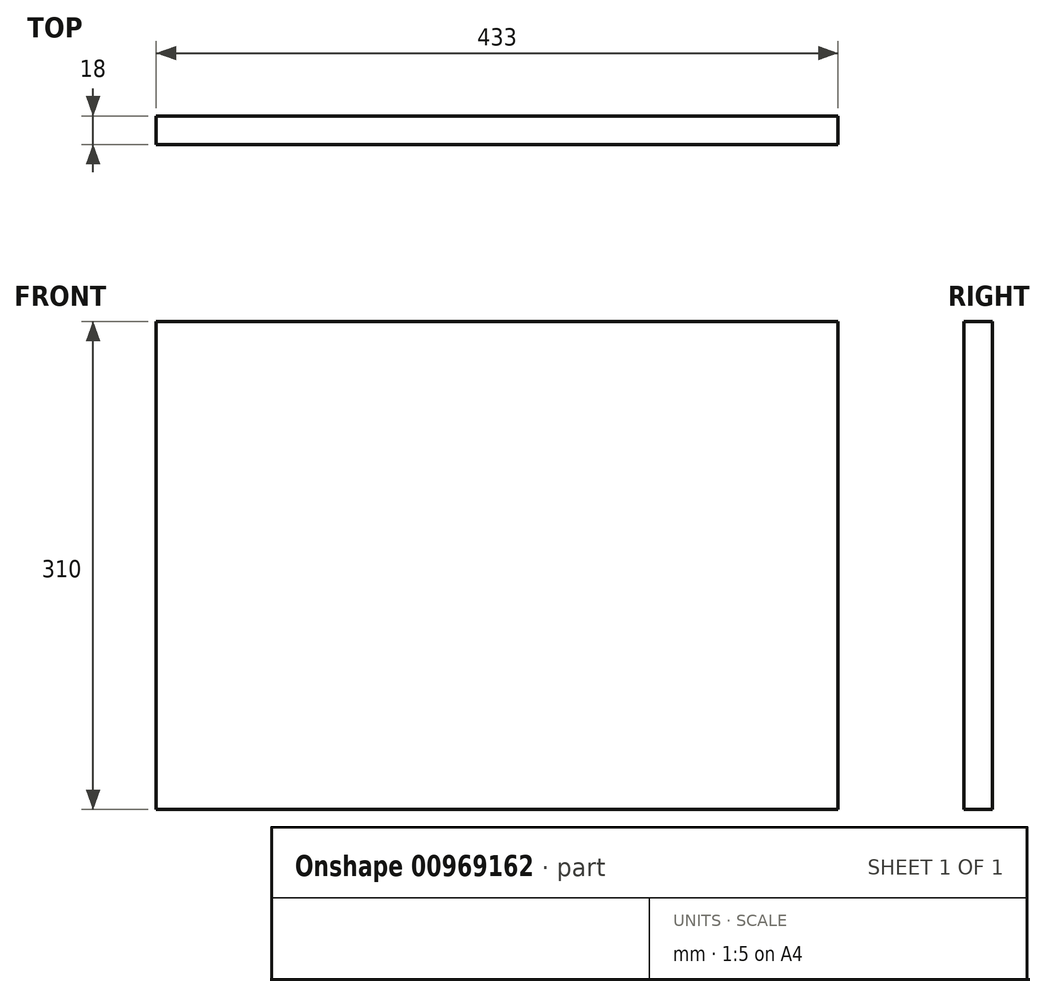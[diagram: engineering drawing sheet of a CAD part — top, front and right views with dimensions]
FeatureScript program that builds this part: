
annotation { "Feature Type Name" : "Feature", "Feature Type Description" : "" }
export const myFeature = defineFeature(function(context is Context, id is Id, definition is map)
    precondition{}
    {
        {
            var Q0;
            Q0=qCreatedBy(makeId("Front.planeOp"),FACE);
            var sketch = newSketch(context, id + "F0", { "sketchPlane" : qUnion([Q0])});
            skLineSegment(sketch, "E0.bottom", {"start": v(0, 0) * mm, "end": v(433, 0) * mm});
            skLineSegment(sketch, "E0.top", {"start": v(0, 310) * mm, "end": v(433, 310) * mm});
            skLineSegment(sketch, "E0.left", {"start": v(0, 0) * mm, "end": v(0, 310) * mm});
            skLineSegment(sketch, "E0.right", {"start": v(433, 0) * mm, "end": v(433, 310) * mm});
            skSolve(sketch);
        }
        {
            var Q0;
            Q0 = qSketchRegion(id + "F0", true);
            extrude(context, id + "F1", {"entities" : qUnion([Q0]), "depth" : 18 * mm, "offsetDistance" : 25 * mm});
        }
    });
